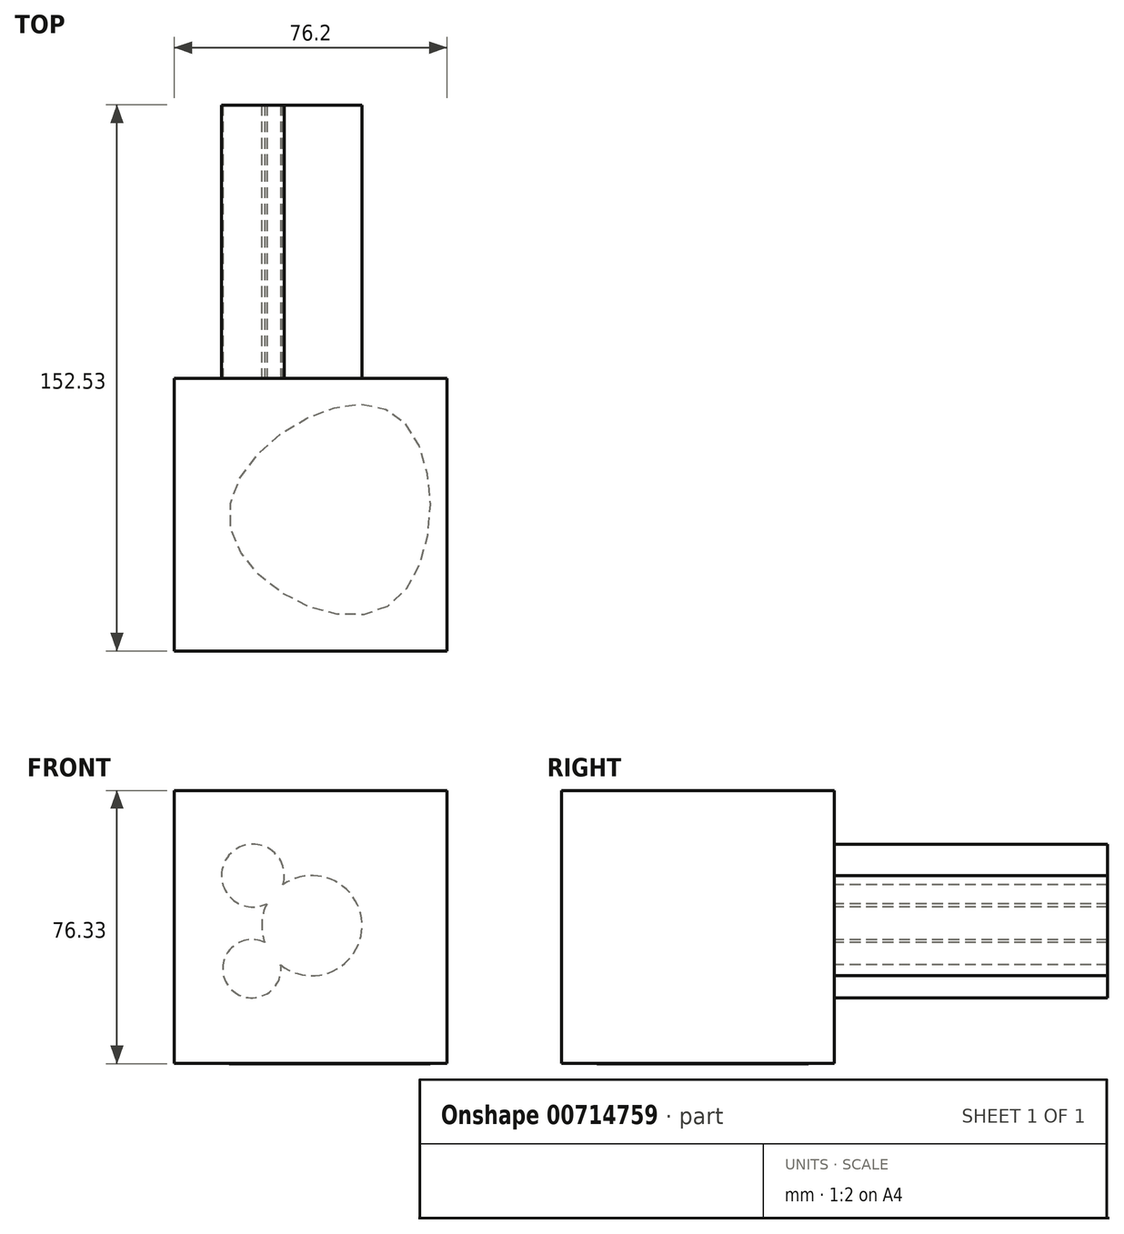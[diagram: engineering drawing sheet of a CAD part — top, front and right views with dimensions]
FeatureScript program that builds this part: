
annotation { "Feature Type Name" : "Feature", "Feature Type Description" : "" }
export const myFeature = defineFeature(function(context is Context, id is Id, definition is map)
    precondition{}
    {
        {
            var Q0;
            Q0=qCreatedBy(makeId("Front.planeOp"),FACE);
            var sketch = newSketch(context, id + "F0", { "sketchPlane" : qUnion([Q0])});
            skLineSegment(sketch, "E0.bottom", {"start": v(-38.45, 37.77) * mm, "end": v(37.75, 37.77) * mm});
            skLineSegment(sketch, "E0.top", {"start": v(-38.45, -38.43) * mm, "end": v(37.75, -38.43) * mm});
            skLineSegment(sketch, "E0.left", {"start": v(-38.45, 37.77) * mm, "end": v(-38.45, -38.43) * mm});
            skLineSegment(sketch, "E0.right", {"start": v(37.75, 37.77) * mm, "end": v(37.75, -38.43) * mm});
            skSolve(sketch);
        }
        {
            var Q0;
            Q0=makeQuery(id+"F0.imprint","IMPRINT",FACE,{"disambiguationData":[TD([[makeQuery(id+"F0.imprint","IMPRINT",EDGE,{"derivedFrom":sQuery(id+"F0.wireOp",EDGE,"E0.bottom")}),-1.0]])]});
            extrude(context, id + "F1", {"entities" : qUnion([Q0]), "depth" : 76.2 * mm, "offsetDistance" : 25.4 * mm});
        }
        {
            var Q0;
            Q0=makeQuery(id+"F1.opExtrude","CAP_FACE",FACE,{"disambiguationData":[OSD([sQuery(id+"F0.wireOp",EDGE,"E0.bottom"),sQuery(id+"F0.wireOp",EDGE,"E0.top"),sQuery(id+"F0.wireOp",EDGE,"E0.left"),sQuery(id+"F0.wireOp",EDGE,"E0.right")])],"isStart":true});
            var sketch = newSketch(context, id + "F2", { "sketchPlane" : qUnion([Q0])});
            skCircle(sketch, "E1", {"center": v(0, 0) * mm, "radius": 14 * mm});
            skSolve(sketch);
        }
        {
            var Q0;
            Q0=makeQuery(id+"F2.imprint","IMPRINT",FACE,{"disambiguationData":[TD([[makeQuery(id+"F2.imprint","IMPRINT",EDGE,{"derivedFrom":sQuery(id+"F2.wireOp",EDGE,"E1")}),1.0]])]});
            extrude(context, id + "F3", {"entities" : qUnion([Q0]), "operationType" : NewBodyOperationType.ADD, "depth" : 76.2 * mm, "offsetDistance" : 25.4 * mm});
        }
        {
            var Q0;
            Q0=makeQuery(id+"F1.opExtrude","CAP_FACE",FACE,{"disambiguationData":[OSD([sQuery(id+"F0.wireOp",EDGE,"E0.bottom"),sQuery(id+"F0.wireOp",EDGE,"E0.top"),sQuery(id+"F0.wireOp",EDGE,"E0.left"),sQuery(id+"F0.wireOp",EDGE,"E0.right")])],"isStart":true});
            var sketch = newSketch(context, id + "F4", { "sketchPlane" : qUnion([Q0])});
            skCircle(sketch, "E2", {"center": v(16.46, 13.99) * mm, "radius": 8.77 * mm});
            skCircle(sketch, "E3", {"center": v(16.75, -12.04) * mm, "radius": 8.14 * mm});
            skSolve(sketch);
        }
        {
            var Q0;
            {var subQ0=sQuery(id+"F4.wireOp",EDGE,"E3");var subQ1=makeQuery(id+"F3.opExtrude","CAP_EDGE",EDGE,{"disambiguationData":[OSD([sQuery(id+"F2.wireOp",EDGE,"E1")])],"isStart":true});var subQ2=makeQuery(id+"F4.imprint","INTERSECT",VERTEX,{"disambiguationData":[OD(0.0)],"derivedFrom":[subQ1,subQ0]});Q0=makeQuery(id+"F4.imprint","IMPRINT",FACE,{"disambiguationData":[TD([[makeQuery(id+"F4.imprint","IMPRINT",EDGE,{"disambiguationData":[TD([[subQ2,1.0]])],"derivedFrom":subQ0}),1.0]])]});}
            var Q1;
            {var subQ0=sQuery(id+"F4.wireOp",EDGE,"E2");var subQ1=makeQuery(id+"F3.opExtrude","CAP_EDGE",EDGE,{"disambiguationData":[OSD([sQuery(id+"F2.wireOp",EDGE,"E1")])],"isStart":true});var subQ2=makeQuery(id+"F4.imprint","INTERSECT",VERTEX,{"disambiguationData":[OD(0.0)],"derivedFrom":[subQ1,subQ0]});Q1=makeQuery(id+"F4.imprint","IMPRINT",FACE,{"disambiguationData":[TD([[makeQuery(id+"F4.imprint","IMPRINT",EDGE,{"disambiguationData":[TD([[subQ2,-1.0]])],"derivedFrom":subQ0}),1.0]])]});}
            extrude(context, id + "F5", {"entities" : qUnion([Q0, Q1]), "operationType" : NewBodyOperationType.ADD, "depth" : 76.2 * mm, "offsetDistance" : 25.4 * mm});
        }
        {
            var Q0;
            {var subQ0=sQuery(id+"F2.wireOp",EDGE,"E1");Q0=makeQuery(id+"F5.boolean.opBoolean","MERGE",FACE,{"derivedFrom":[makeQuery(id+"F3.opExtrude","CAP_FACE",FACE,{"disambiguationData":[OSD([subQ0])],"isStart":false}),makeQuery(id+"F5.opExtrude","CAP_FACE",FACE,{"disambiguationData":[OSD([subQ0,sQuery(id+"F4.wireOp",EDGE,"E2")])],"isStart":false}),makeQuery(id+"F5.opExtrude","CAP_FACE",FACE,{"disambiguationData":[OSD([subQ0,sQuery(id+"F4.wireOp",EDGE,"E3")])],"isStart":false})]});}
            extrude(context, id + "F6", {"entities" : qUnion([Q0]), "operationType" : NewBodyOperationType.ADD, "depth" : 0.13 * mm, "offsetDistance" : 25.4 * mm});
        }
        {
            var Q0;
            Q0=makeQuery(id+"F1.opExtrude","SWEPT_FACE",FACE,{"disambiguationData":[OSD([sQuery(id+"F0.wireOp",EDGE,"E0.top")])]});
            var sketch = newSketch(context, id + "F7", { "sketchPlane" : qUnion([Q0])});
            skFitSpline(sketch, "E4", {"points": [v(21.1, 63.79) * mm, v(-23.08, 38.38) * mm, v(21.96, 9.31) * mm, v(21.1, 63.79) * mm]});
            skSolve(sketch);
        }
        {
            var Q0;
            Q0=makeQuery(id+"F7.imprint","IMPRINT",FACE,{"disambiguationData":[TD([[makeQuery(id+"F7.imprint","IMPRINT",EDGE,{"derivedFrom":sQuery(id+"F7.wireOp",EDGE,"E4")}),1.0]])]});
            extrude(context, id + "F8", {"entities" : qUnion([Q0]), "operationType" : NewBodyOperationType.ADD, "depth" : 0.13 * mm, "offsetDistance" : 25.4 * mm});
        }
    });
